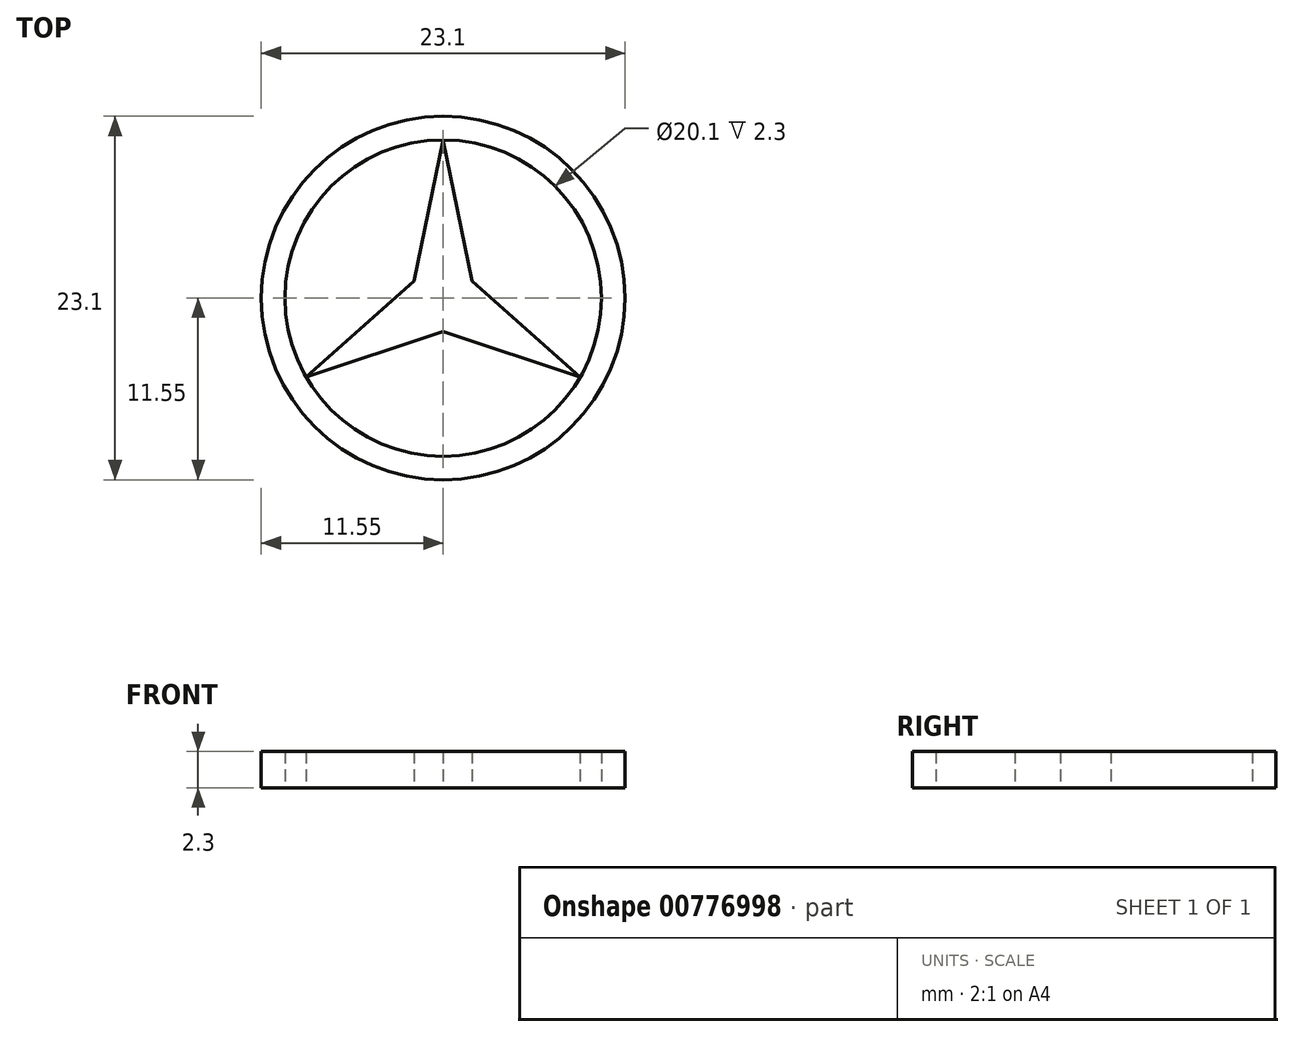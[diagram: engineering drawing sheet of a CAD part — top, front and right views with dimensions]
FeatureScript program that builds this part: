
annotation { "Feature Type Name" : "Feature", "Feature Type Description" : "" }
export const myFeature = defineFeature(function(context is Context, id is Id, definition is map)
    precondition{}
    {
        {
            var Q0;
            Q0=qCreatedBy(makeId("Top.planeOp"),FACE);
            var sketch = newSketch(context, id + "F0", { "sketchPlane" : qUnion([Q0])});
            skCircle(sketch, "E0", {"center": v(0, 0) * mm, "radius": 11.55 * mm});
            skCircle(sketch, "E1", {"center": v(0, 0) * mm, "radius": 10.05 * mm});
            skLineSegment(sketch, "E2", {"start": v(0, 20.4) * mm, "end": v(0, 0) * mm, "construction": true});
            skLineSegment(sketch, "E3", {"start": v(0, 0) * mm, "end": v(17.67, -10.2) * mm, "construction": true});
            skLineSegment(sketch, "E4", {"start": v(0, 0) * mm, "end": v(-17.67, -10.2) * mm, "construction": true});
            skLineSegment(sketch, "E5", {"start": v(0, 10.05) * mm, "end": v(-1.85, 1.07) * mm});
            skLineSegment(sketch, "E6", {"start": v(-1.85, 1.07) * mm, "end": v(-8.7, -5.03) * mm});
            skLineSegment(sketch, "E7", {"start": v(-8.7, -5.03) * mm, "end": v(0, -2.14) * mm});
            skLineSegment(sketch, "E8", {"start": v(0, -2.14) * mm, "end": v(8.7, -5.03) * mm});
            skLineSegment(sketch, "E9", {"start": v(8.7, -5.03) * mm, "end": v(1.85, 1.07) * mm});
            skLineSegment(sketch, "E10", {"start": v(1.85, 1.07) * mm, "end": v(0, 10.05) * mm});
            skSolve(sketch);
        }
        {
            var Q0;
            Q0=makeQuery(id+"F0.imprint","IMPRINT",FACE,{"disambiguationData":[TD([[makeQuery(id+"F0.imprint","IMPRINT",EDGE,{"derivedFrom":sQuery(id+"F0.wireOp",EDGE,"E0")}),1.0]])]});
            var Q1;
            Q1=makeQuery(id+"F0.imprint","IMPRINT",FACE,{"disambiguationData":[TD([[makeQuery(id+"F0.imprint","IMPRINT",EDGE,{"derivedFrom":sQuery(id+"F0.wireOp",EDGE,"E5")}),1.0]])]});
            extrude(context, id + "F1", {"entities" : qUnion([Q0, Q1]), "depth" : 2.3 * mm, "offsetDistance" : 25 * mm});
        }
    });
